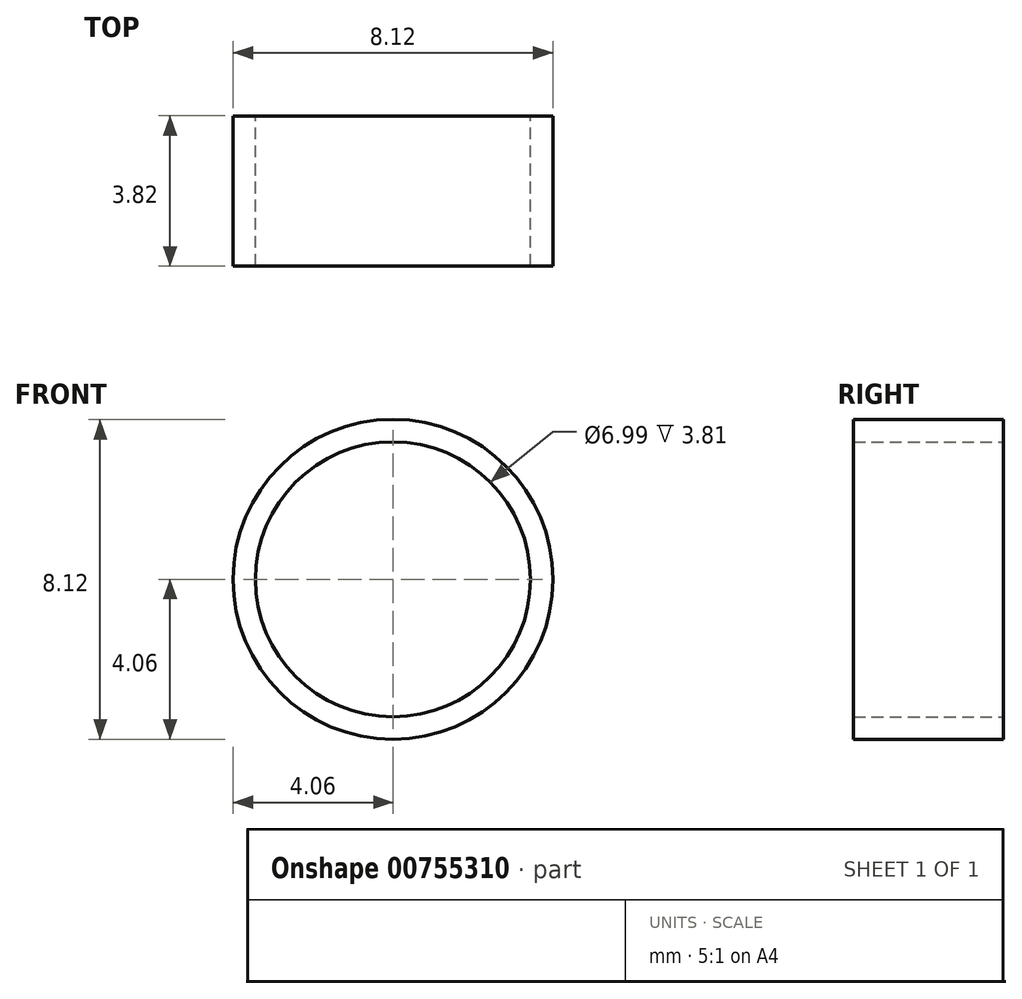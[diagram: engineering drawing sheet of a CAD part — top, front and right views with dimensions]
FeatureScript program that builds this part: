
annotation { "Feature Type Name" : "Feature", "Feature Type Description" : "" }
export const myFeature = defineFeature(function(context is Context, id is Id, definition is map)
    precondition{}
    {
        {
            var Q0;
            Q0=qCreatedBy(makeId("Front.planeOp"),FACE);
            var sketch = newSketch(context, id + "F0", { "sketchPlane" : qUnion([Q0])});
            skCircle(sketch, "E0", {"center": v(0, 0) * mm, "radius": 3.5 * mm});
            skCircle(sketch, "E1", {"center": v(0, 0) * mm, "radius": 4.06 * mm});
            skSolve(sketch);
        }
        {
            var Q0;
            Q0=makeQuery(id+"F0.imprint","IMPRINT",FACE,{"disambiguationData":[TD([[makeQuery(id+"F0.imprint","IMPRINT",EDGE,{"derivedFrom":sQuery(id+"F0.wireOp",EDGE,"E0")}),-1.0]])]});
            extrude(context, id + "F1", {"entities" : qUnion([Q0]), "depth" : 3.8 * mm, "offsetDistance" : 25.4 * mm, "symmetric" : true});
        }
    });
